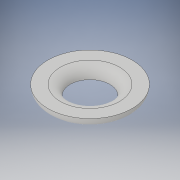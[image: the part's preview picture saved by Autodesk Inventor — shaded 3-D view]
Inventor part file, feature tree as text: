
AUTODESK INVENTOR PART (.ipt)
format: ipt  version: 2019 (Build 230136000, 136)  size: 134,656 bytes
history: native  units: mm
features: fillet x2, other x1, extrude x1, sketch x1
ambient origin geometry x8: Origin, YZ Plane, XZ Plane, XY Plane, X Axis, Y Axis, Z Axis, Center Point
bodies: Body1 (feature_tree)
feature tree (5):
  other  "Sólido1"
  extrude  "Extrusión1"  Depth=2.0mm
  fillet  "Empalme1"  Radius=2.0mm
  fillet  "Empalme2"  Radius=2.0mm
  sketch  "Boceto1"  dims[d0=8.0mm d1=17.0mm d2=2.0mm d3=0.0mm d4=2.0mm d5=2.0mm]
